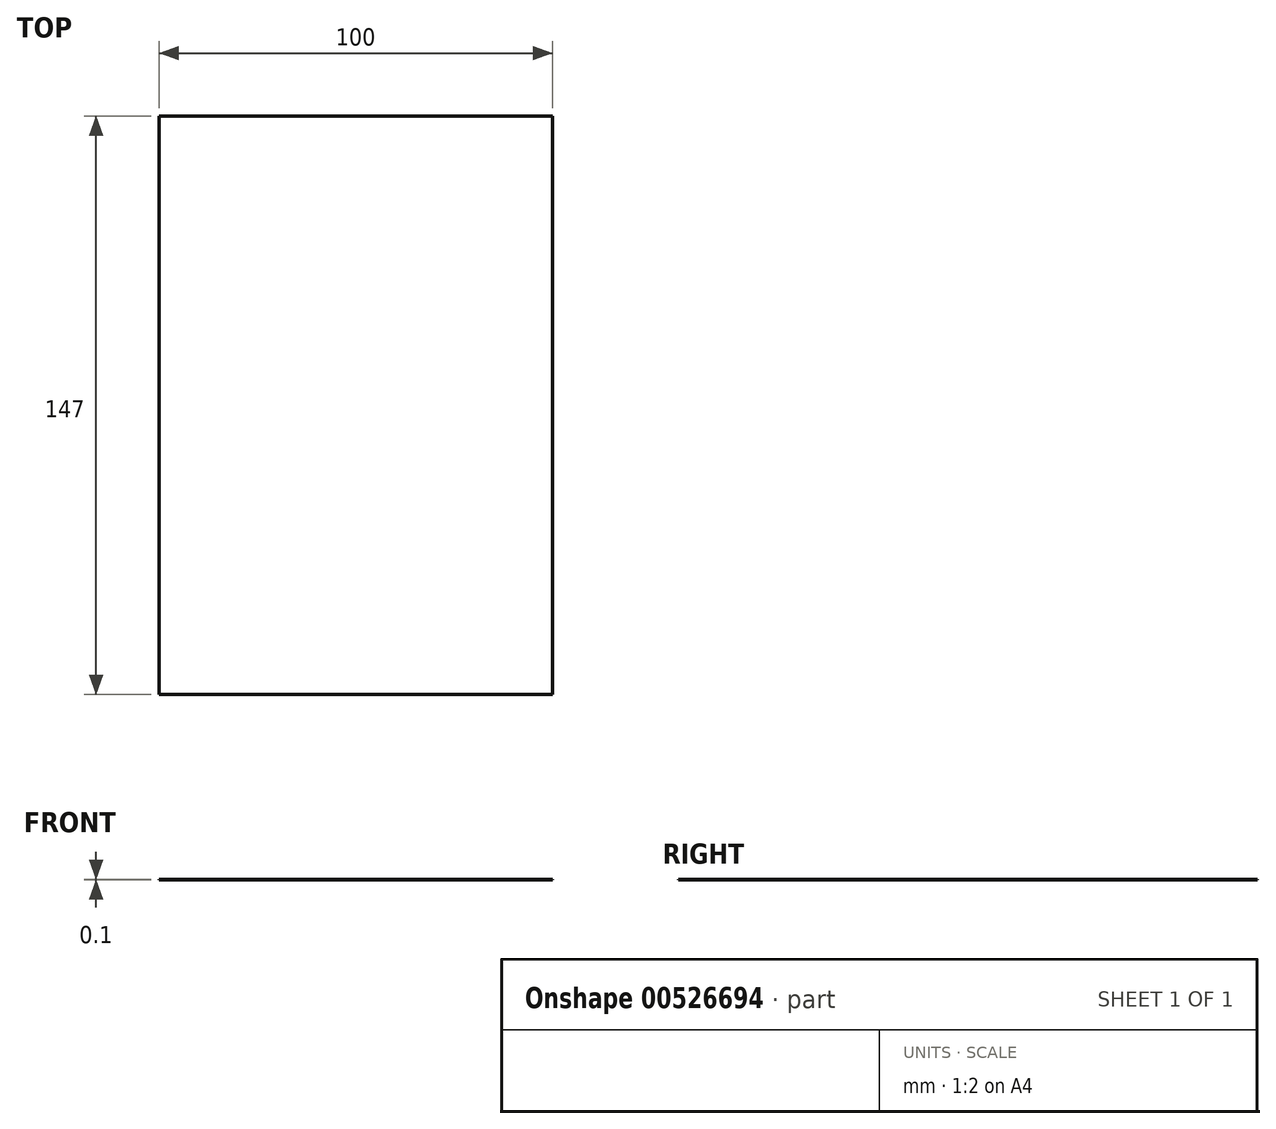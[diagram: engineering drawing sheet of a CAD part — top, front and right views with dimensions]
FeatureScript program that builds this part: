
annotation { "Feature Type Name" : "Feature", "Feature Type Description" : "" }
export const myFeature = defineFeature(function(context is Context, id is Id, definition is map)
    precondition{}
    {
        {
            var Q0;
            Q0=qCreatedBy(makeId("Top.planeOp"),FACE);
            var sketch = newSketch(context, id + "F0", { "sketchPlane" : qUnion([Q0])});
            skLineSegment(sketch, "E0.bottom", {"start": v(-0.77, 10.7) * mm, "end": v(-100.77, 10.7) * mm});
            skLineSegment(sketch, "E0.top", {"start": v(-0.77, -136.3) * mm, "end": v(-100.77, -136.3) * mm});
            skLineSegment(sketch, "E0.left", {"start": v(-0.77, 10.7) * mm, "end": v(-0.77, -136.3) * mm});
            skLineSegment(sketch, "E0.right", {"start": v(-100.77, 10.7) * mm, "end": v(-100.77, -136.3) * mm});
            skPoint(sketch, "E0.middle", {"position": v(-50.77, -62.8) * mm});
            skSolve(sketch);
        }
        {
            var Q0;
            Q0 = qSketchRegion(id + "F0", true);
            extrude(context, id + "F1", {"entities" : qUnion([Q0]), "depth" : 0.1 * mm, "offsetDistance" : 25 * mm});
        }
    });
